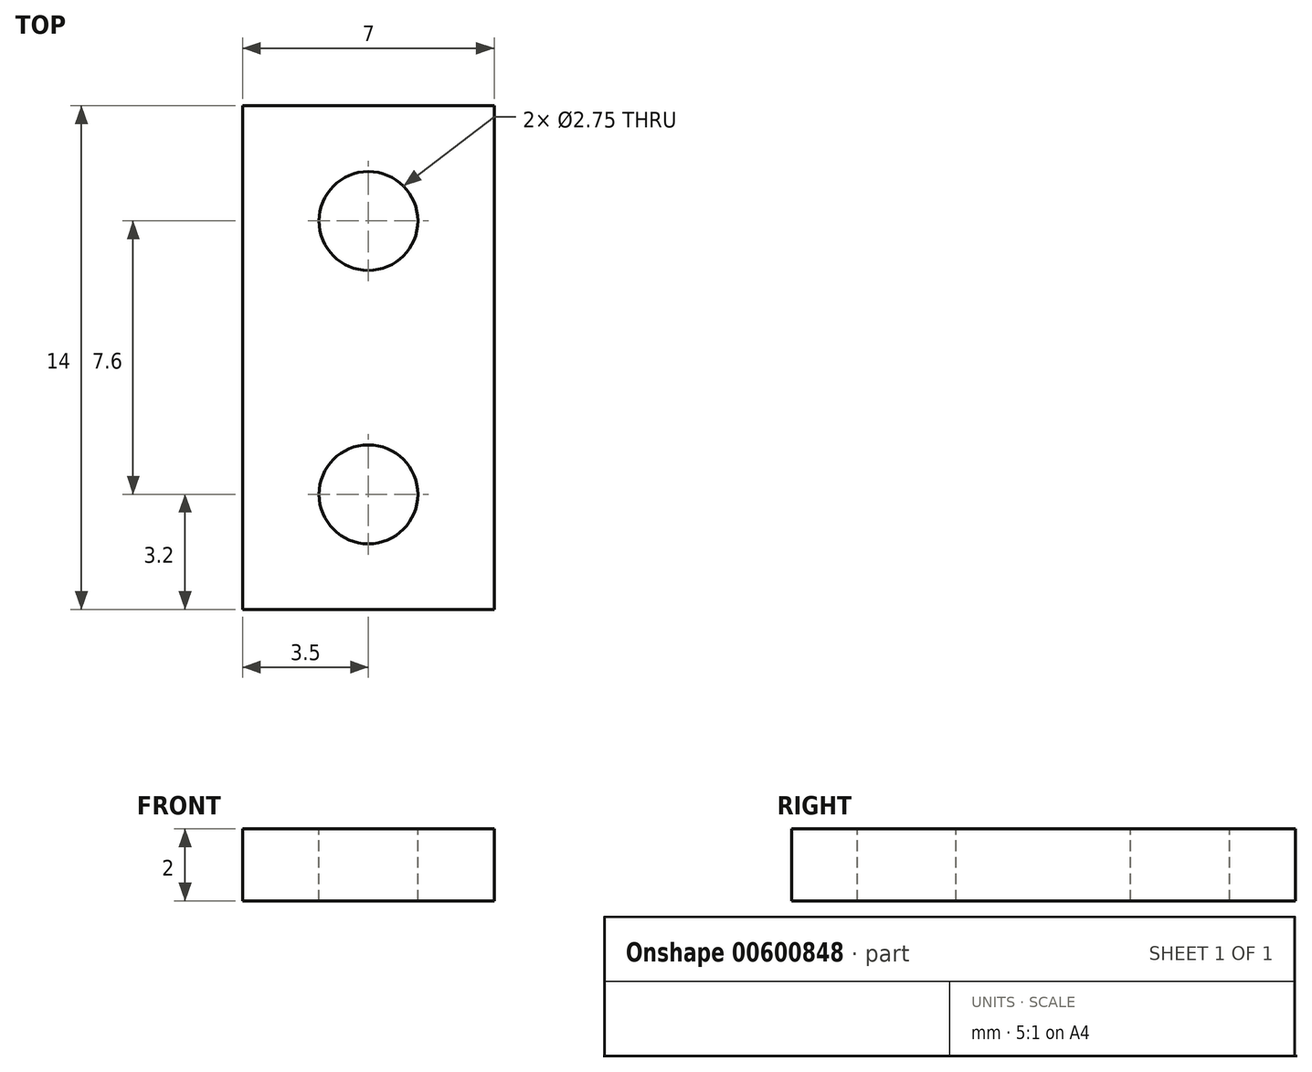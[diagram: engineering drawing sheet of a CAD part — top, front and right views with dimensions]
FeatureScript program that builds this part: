
annotation { "Feature Type Name" : "Feature", "Feature Type Description" : "" }
export const myFeature = defineFeature(function(context is Context, id is Id, definition is map)
    precondition{}
    {
        {
            var Q0;
            Q0=qCreatedBy(makeId("Top.planeOp"),FACE);
            var sketch = newSketch(context, id + "F0", { "sketchPlane" : qUnion([Q0])});
            skLineSegment(sketch, "E0.bottom", {"start": v(0, 0) * mm, "end": v(7, 0) * mm});
            skLineSegment(sketch, "E0.top", {"start": v(0, 14) * mm, "end": v(7, 14) * mm});
            skLineSegment(sketch, "E0.left", {"start": v(0, 0) * mm, "end": v(0, 14) * mm});
            skLineSegment(sketch, "E0.right", {"start": v(7, 0) * mm, "end": v(7, 14) * mm});
            skSolve(sketch);
        }
        {
            var Q0;
            Q0=makeQuery(id+"F0.imprint","IMPRINT",FACE,{"disambiguationData":[TD([[makeQuery(id+"F0.imprint","IMPRINT",EDGE,{"derivedFrom":sQuery(id+"F0.wireOp",EDGE,"E0.bottom")}),1.0]])]});
            extrude(context, id + "F1", {"entities" : qUnion([Q0]), "depth" : 2 * mm, "offsetDistance" : 25 * mm});
        }
        {
            var Q0;
            Q0=makeQuery(id+"F1.opExtrude","CAP_FACE",FACE,{"disambiguationData":[OSD([sQuery(id+"F0.wireOp",EDGE,"E0.bottom"),sQuery(id+"F0.wireOp",EDGE,"E0.top"),sQuery(id+"F0.wireOp",EDGE,"E0.left"),sQuery(id+"F0.wireOp",EDGE,"E0.right")])],"isStart":false});
            var sketch = newSketch(context, id + "F2", { "sketchPlane" : qUnion([Q0])});
            skCircle(sketch, "E1", {"center": v(3.5, 3.2) * mm, "radius": 1.38 * mm});
            skSolve(sketch);
        }
        {
            var Q0;
            Q0=makeQuery(id+"F2.imprint","IMPRINT",FACE,{"disambiguationData":[TD([[makeQuery(id+"F2.imprint","IMPRINT",EDGE,{"derivedFrom":sQuery(id+"F2.wireOp",EDGE,"E1")}),-1.0]])]});
            var sketch = newSketch(context, id + "F3", { "sketchPlane" : qUnion([Q0])});
            skCircle(sketch, "E2", {"center": v(3.5, 10.8) * mm, "radius": 1.38 * mm});
            skSolve(sketch);
        }
        {
            var Q0;
            Q0=makeQuery(id+"F2.imprint","IMPRINT",FACE,{"disambiguationData":[TD([[makeQuery(id+"F2.imprint","IMPRINT",EDGE,{"derivedFrom":sQuery(id+"F2.wireOp",EDGE,"E1")}),1.0]])]});
            extrude(context, id + "F4", {"entities" : qUnion([Q0]), "operationType" : NewBodyOperationType.REMOVE, "oppositeDirection" : true, "depth" : 3 * mm, "offsetDistance" : 25 * mm});
        }
        {
            var Q0;
            Q0=makeQuery(id+"F3.imprint","IMPRINT",FACE,{"disambiguationData":[TD([[makeQuery(id+"F3.imprint","IMPRINT",EDGE,{"derivedFrom":sQuery(id+"F3.wireOp",EDGE,"E2")}),1.0]])]});
            extrude(context, id + "F5", {"entities" : qUnion([Q0]), "operationType" : NewBodyOperationType.REMOVE, "oppositeDirection" : true, "depth" : 3 * mm, "offsetDistance" : 25 * mm});
        }
    });
